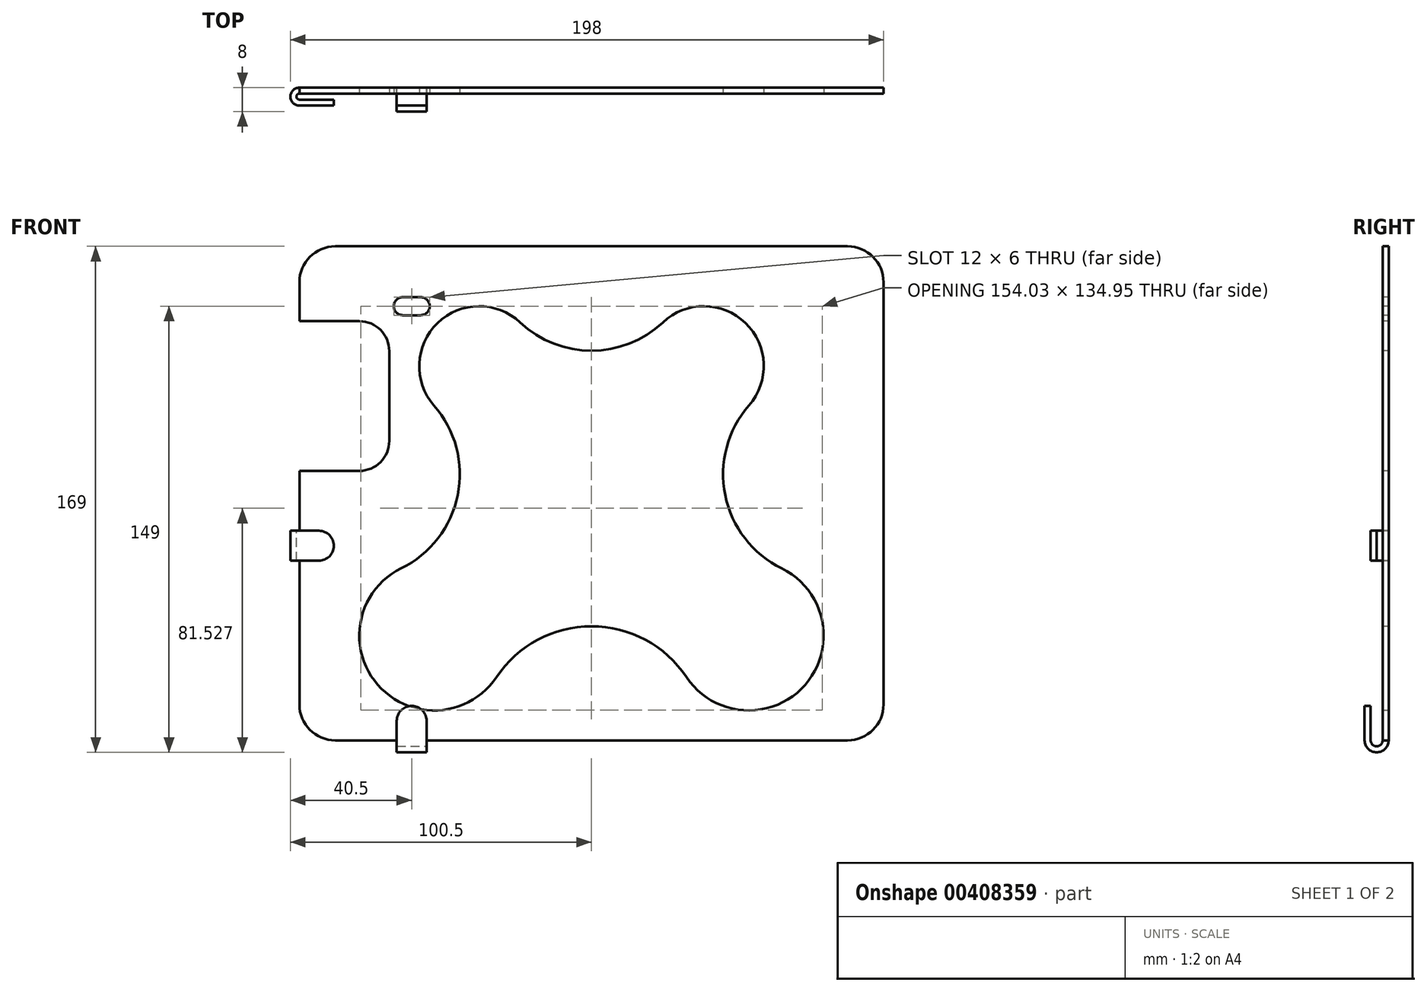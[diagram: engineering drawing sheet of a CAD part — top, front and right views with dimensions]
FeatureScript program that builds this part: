
annotation { "Feature Type Name" : "Feature", "Feature Type Description" : "" }
export const myFeature = defineFeature(function(context is Context, id is Id, definition is map)
    precondition{}
    {
        {
            var Q0;
            Q0=qCreatedBy(makeId("Front.planeOp"),FACE);
            var sketch = newSketch(context, id + "F0", { "sketchPlane" : qUnion([Q0])});
            skLineSegment(sketch, "E0.bottom", {"start": v(-97.5, 82.5) * mm, "end": v(97.5, 82.5) * mm});
            skLineSegment(sketch, "E0.top", {"start": v(-97.5, -82.5) * mm, "end": v(97.5, -82.5) * mm});
            skLineSegment(sketch, "E0.left", {"start": v(-97.5, 82.5) * mm, "end": v(-97.5, -82.5) * mm});
            skLineSegment(sketch, "E0.right", {"start": v(97.5, 82.5) * mm, "end": v(97.5, -82.5) * mm});
            skPoint(sketch, "E0.middle", {"position": v(0, 0) * mm});
            skSolve(sketch);
        }
        {
            var Q0;
            Q0 = qSketchRegion(id + "F0", true);
            extrude(context, id + "F1", {"entities" : qUnion([Q0]), "depth" : 2 * mm});
        }
        {
            var Q0;
            Q0=makeQuery(id+"F1.opExtrude","SWEPT_EDGE",EDGE,{"disambiguationData":[OSD([sQuery(id+"F0.wireOp",EDGE,"E0.bottom"),sQuery(id+"F0.wireOp",EDGE,"E0.right")])]});
            var Q1;
            Q1=makeQuery(id+"F1.opExtrude","SWEPT_EDGE",EDGE,{"disambiguationData":[OSD([sQuery(id+"F0.wireOp",EDGE,"E0.top"),sQuery(id+"F0.wireOp",EDGE,"E0.right")])]});
            var Q2;
            Q2=makeQuery(id+"F1.opExtrude","SWEPT_EDGE",EDGE,{"disambiguationData":[OSD([sQuery(id+"F0.wireOp",EDGE,"E0.bottom"),sQuery(id+"F0.wireOp",EDGE,"E0.left")])]});
            var Q3;
            Q3=makeQuery(id+"F1.opExtrude","SWEPT_EDGE",EDGE,{"disambiguationData":[OSD([sQuery(id+"F0.wireOp",EDGE,"E0.top"),sQuery(id+"F0.wireOp",EDGE,"E0.left")])]});
            fillet(context, id + "F2", {"entities" : qUnion([Q0, Q1, Q2, Q3]), "radius" : 12 * mm, "tangentPropagation" : true, "allowEdgeOverflow" : false});
        }
        {
            var Q0;
            Q0=makeQuery(id+"F1.opExtrude","CAP_FACE",FACE,{"disambiguationData":[OSD([sQuery(id+"F0.wireOp",EDGE,"E0.bottom"),sQuery(id+"F0.wireOp",EDGE,"E0.top"),sQuery(id+"F0.wireOp",EDGE,"E0.left"),sQuery(id+"F0.wireOp",EDGE,"E0.right")])],"isStart":false});
            var sketch = newSketch(context, id + "F3", { "sketchPlane" : qUnion([Q0])});
            skLineSegment(sketch, "E1.bottom", {"start": v(-97.5, 57.5) * mm, "end": v(-67.5, 57.5) * mm});
            skLineSegment(sketch, "E1.top", {"start": v(-97.5, 7.5) * mm, "end": v(-67.5, 7.5) * mm});
            skLineSegment(sketch, "E1.left", {"start": v(-97.5, 57.5) * mm, "end": v(-97.5, 7.5) * mm});
            skLineSegment(sketch, "E1.right", {"start": v(-67.5, 57.5) * mm, "end": v(-67.5, 7.5) * mm});
            skSolve(sketch);
        }
        {
            var Q0;
            Q0 = qSketchRegion(id + "F3", true);
            extrude(context, id + "F4", {"entities" : qUnion([Q0]), "operationType" : NewBodyOperationType.REMOVE, "endBound" : BoundingType.THROUGH_ALL, "oppositeDirection" : true, "depth" : 25 * mm});
        }
        {
            var Q0;
            Q0=makeQuery(id+"F1.opExtrude","CAP_FACE",FACE,{"disambiguationData":[OSD([sQuery(id+"F0.wireOp",EDGE,"E0.bottom"),sQuery(id+"F0.wireOp",EDGE,"E0.top"),sQuery(id+"F0.wireOp",EDGE,"E0.left"),sQuery(id+"F0.wireOp",EDGE,"E0.right")])],"isStart":false});
            var sketch = newSketch(context, id + "F5", { "sketchPlane" : qUnion([Q0])});
            skLineSegment(sketch, "E2.bottom", {"start": v(-63, 65.5) * mm, "end": v(-57, 65.5) * mm});
            skLineSegment(sketch, "E2.top", {"start": v(-63, 59.5) * mm, "end": v(-57, 59.5) * mm});
            skArc(sketch, "E3", {"start": v(-63, 65.5) * mm, "mid": v(-66, 62.5) * mm, "end": v(-63, 59.5) * mm});
            skArc(sketch, "E4", {"start": v(-57, 59.5) * mm, "mid": v(-54, 62.5) * mm, "end": v(-57, 65.5) * mm});
            skPoint(sketch, "E5.center.orphan", {"position": v(74.22, 62.5) * mm});
            skPoint(sketch, "E5.end.orphan", {"position": v(74.19, 59.5) * mm});
            skPoint(sketch, "E5.start.orphan", {"position": v(74.26, 65.5) * mm});
            skLineSegment(sketch, "E6", {"start": v(-60, 65.5) * mm, "end": v(-60, 59.5) * mm, "construction": true});
            skSolve(sketch);
        }
        {
            var Q0;
            Q0 = qSketchRegion(id + "F5", true);
            extrude(context, id + "F6", {"entities" : qUnion([Q0]), "operationType" : NewBodyOperationType.REMOVE, "endBound" : BoundingType.THROUGH_ALL, "oppositeDirection" : true, "depth" : 25 * mm});
        }
        {
            var Q0;
            Q0=qCreatedBy(makeId("Top.planeOp"),FACE);
            cPlane(context, id + "F7", {"entities" : qUnion([Q0]), "cplaneType" : CPlaneType.OFFSET, "offset" : 12.5 * mm, "oppositeDirection" : true, "width" : 150 * mm, "height" : 150 * mm});
        }
        {
            var Q0;
            Q0=makeQuery(id+"F4.boolean.opBoolean","COPY",EDGE,{"derivedFrom":makeQuery(id+"F4.opExtrude","SWEPT_EDGE",EDGE,{"disambiguationData":[OSD([sQuery(id+"F3.wireOp",EDGE,"E1.bottom"),sQuery(id+"F3.wireOp",EDGE,"E1.right")])]})});
            var Q1;
            Q1=makeQuery(id+"F4.boolean.opBoolean","COPY",EDGE,{"derivedFrom":makeQuery(id+"F4.opExtrude","SWEPT_EDGE",EDGE,{"disambiguationData":[OSD([sQuery(id+"F3.wireOp",EDGE,"E1.top"),sQuery(id+"F3.wireOp",EDGE,"E1.right")])]})});
            fillet(context, id + "F8", {"entities" : qUnion([Q0, Q1]), "radius" : 10 * mm, "tangentPropagation" : true, "allowEdgeOverflow" : false});
        }
        {
            var Q0;
            Q0=qCreatedBy(id+"F7.planeOp",FACE);
            var sketch = newSketch(context, id + "F9", { "sketchPlane" : qUnion([Q0])});
            skLineSegment(sketch, "E7", {"start": v(-86, -4) * mm, "end": v(-86, -6) * mm});
            skLineSegment(sketch, "E8", {"start": v(-86, -6) * mm, "end": v(-97.5, -6) * mm});
            skArc(sketch, "E9", {"start": v(-97.5, -2) * mm, "mid": v(-98.5, -3) * mm, "end": v(-97.5, -4) * mm});
            skArc(sketch, "E10", {"start": v(-97.5, 0) * mm, "mid": v(-100.5, -3) * mm, "end": v(-97.5, -6) * mm});
            skPoint(sketch, "E11.orphan", {"position": v(-99.78, 0) * mm});
            skLineSegment(sketch, "E12.trimOffspring", {"start": v(-97.5, -2) * mm, "end": v(-97.5, 0) * mm});
            skLineSegment(sketch, "E13", {"start": v(-97.5, -4) * mm, "end": v(-86, -4) * mm});
            skPoint(sketch, "E14.orphan", {"position": v(-56.06, -4) * mm});
            skSolve(sketch);
        }
        {
            var Q0;
            Q0 = qSketchRegion(id + "F9", true);
            extrude(context, id + "F10", {"entities" : qUnion([Q0]), "operationType" : NewBodyOperationType.ADD, "oppositeDirection" : true, "depth" : 10 * mm});
        }
        {
            var Q0;
            Q0=makeQuery(id+"F10.opExtrude","CAP_EDGE",EDGE,{"disambiguationData":[OSD([sQuery(id+"F9.wireOp",EDGE,"E7")])],"isStart":true});
            var Q1;
            Q1=makeQuery(id+"F10.opExtrude","CAP_EDGE",EDGE,{"disambiguationData":[OSD([sQuery(id+"F9.wireOp",EDGE,"E7")])],"isStart":false});
            fillet(context, id + "F11", {"entities" : qUnion([Q0, Q1]), "radius" : 5 * mm, "tangentPropagation" : true, "allowEdgeOverflow" : false});
        }
        {
            var Q0;
            Q0=qCreatedBy(makeId("Right.planeOp"),FACE);
            cPlane(context, id + "F12", {"entities" : qUnion([Q0]), "cplaneType" : CPlaneType.OFFSET, "offset" : 55 * mm, "oppositeDirection" : true, "width" : 150 * mm, "height" : 150 * mm});
        }
        {
            var Q0;
            Q0=qCreatedBy(id+"F12.planeOp",FACE);
            var sketch = newSketch(context, id + "F13", { "sketchPlane" : qUnion([Q0])});
            skArc(sketch, "E15", {"start": v(-6, -82.5) * mm, "mid": v(-4, -84.5) * mm, "end": v(-2, -82.5) * mm});
            skArc(sketch, "E16", {"start": v(-8, -82.5) * mm, "mid": v(-4, -86.5) * mm, "end": v(0, -82.5) * mm});
            skLineSegment(sketch, "E17", {"start": v(-6, -71) * mm, "end": v(-8, -71) * mm});
            skLineSegment(sketch, "E18", {"start": v(-8, -71) * mm, "end": v(-8, -82.5) * mm});
            skLineSegment(sketch, "E19", {"start": v(-6, -82.5) * mm, "end": v(-6, -71) * mm});
            skLineSegment(sketch, "E20", {"start": v(0, -82.5) * mm, "end": v(-2, -82.5) * mm});
            skSolve(sketch);
        }
        {
            var Q0;
            Q0 = qSketchRegion(id + "F13", true);
            extrude(context, id + "F14", {"entities" : qUnion([Q0]), "operationType" : NewBodyOperationType.ADD, "oppositeDirection" : true, "depth" : 10 * mm});
        }
        {
            var Q0;
            Q0=makeQuery(id+"F14.opExtrude","CAP_EDGE",EDGE,{"disambiguationData":[OSD([sQuery(id+"F13.wireOp",EDGE,"E17")])],"isStart":false});
            var Q1;
            Q1=makeQuery(id+"F14.opExtrude","CAP_EDGE",EDGE,{"disambiguationData":[OSD([sQuery(id+"F13.wireOp",EDGE,"E17")])],"isStart":true});
            fillet(context, id + "F15", {"entities" : qUnion([Q0, Q1]), "radius" : 5 * mm, "tangentPropagation" : true, "allowEdgeOverflow" : false});
        }
        {
            var Q0;
            Q0=makeQuery(id+"F1.opExtrude","CAP_FACE",FACE,{"disambiguationData":[OSD([sQuery(id+"F0.wireOp",EDGE,"E0.bottom"),sQuery(id+"F0.wireOp",EDGE,"E0.top"),sQuery(id+"F0.wireOp",EDGE,"E0.left"),sQuery(id+"F0.wireOp",EDGE,"E0.right")])],"isStart":false});
            var sketch = newSketch(context, id + "F16", { "sketchPlane" : qUnion([Q0])});
            skArc(sketch, "E21", {"start": v(-63.52, -25.06) * mm, "mid": v(-71.3, -63.98) * mm, "end": v(-31.7, -61.37) * mm});
            skArc(sketch, "E22", {"start": v(-23.82, 57.1) * mm, "mid": v(-51.39, 56.9) * mm, "end": v(-52.57, 29.36) * mm});
            skArc(sketch, "E23", {"start": v(52.57, 29.36) * mm, "mid": v(51.39, 56.9) * mm, "end": v(23.82, 57.1) * mm});
            skArc(sketch, "E24", {"start": v(31.7, -61.37) * mm, "mid": v(71.3, -63.98) * mm, "end": v(63.52, -25.06) * mm});
            skArc(sketch, "E25", {"start": v(-63.52, -25.06) * mm, "mid": v(-44.64, -0.55) * mm, "end": v(-52.57, 29.36) * mm});
            skArc(sketch, "E26", {"start": v(31.7, -61.37) * mm, "mid": v(0, -44.4) * mm, "end": v(-31.7, -61.37) * mm});
            skArc(sketch, "E27", {"start": v(52.57, 29.36) * mm, "mid": v(44.64, -0.55) * mm, "end": v(63.52, -25.06) * mm});
            skArc(sketch, "E28", {"start": v(-23.82, 57.1) * mm, "mid": v(0, 47.67) * mm, "end": v(23.82, 57.1) * mm});
            skSolve(sketch);
        }
        {
            var Q0;
            Q0 = qSketchRegion(id + "F16", true);
            extrude(context, id + "F17", {"entities" : qUnion([Q0]), "operationType" : NewBodyOperationType.REMOVE, "oppositeDirection" : true, "depth" : 2 * mm});
        }
    });
